# Revit family: 62172
name_source: partatom
category: Lighting Fixtures
revit_build: Autodesk Revit 2018 (Build: 20170223_1515(x64)
units: mm (PartAtom-declared; Revit-internal decimal feet)

## family parameters
Cut with Voids When Loaded = No
Host = Face
Light Source = Yes
OmniClass Number = 23.80.70.00
OmniClass Title = Lighting
Part Type = Normal
Room Calculation Point = No
Round Connector Dimension = Use Diameter
Shared = No

## types (1)
- 0062172 KUBIXX 4000K 47KLM AISLE  SSA N
    Apparent Load = 276 VA
    Assembly Code = D5020200
    AssetType = Fixed
    ClassificationName = Uniclass2015
    ClassificationValue = EF_70_80
    Color Filter = 16777215
    Cost = 0 $
    Default Elevation = 1219 mm
    Description = Logistics and Industry high bay luminaire with wide optics to provide homogenous light distribution for open space areas. 48300lumens, 276W, 175lm/W, 4000K, CRI80, wide beam optic, SylSmart SSA dimmable, 3 step MacAdam ellipse, grey finish (RAL7012), Class 1, 220-240V, IP65, IK06.
    Dimming Lamp Color Temperature Shift = <None>
    DocumentationLiterature = http://www.sylvania-lighting.com
    ElectricShockClassification = 175
    Emit Shape Visible in Rendering = No
    Emit from Circle Diameter = 610 mm
    IfcExportAs = Class I
    IfcExportType = IfcLightFixtureType
    ImpactProtectionIndex = IfcLightFixtureType
    IngressProtection = IfcLightFixtureType
    InputNominalFrequency = 4000
    InputVoltage = 0
    LampColourRenderingIndex = 16500
    LampColourTemperature = LED
    LampMacAdamStep = 80
    LampNominalLuminous = 4000 K
    LightOutputRatio = LED
    LuminaireType = 0
    ManufacturerName = 175 lm/W
    Material = Feilo Sylvania
    Material_1_SYL = <By Category>
    Material_2_SYL = <By Category>
    Material_3_SYL = <By Category>
    Material_4_SYL = <By Category>
    Model = KubiXx 4000K 47KLM AISLE  SSA N
    ModelNumber = 0062172
    ModelReference = KubiXx 4000K 47KLM AISLE  SSA N
    Name = KubiXx 4000K 47KLM AISLE  SSA N
    NominalDepth = 650 mm  [stored 2.13255 ft]
    NominalHeight = 94 mm  [stored 0.308399 ft]
    NominalLength = 460 mm  [stored 1.50919 ft]
    Photometric Web File = 0062172.IES
    PowerConsumption = Lighting
    PowerFactor = 0
    Suspension height = 3000 mm  [stored 9.84252 ft]
    Tilt Angle = -90.00°
    Total Length = 732 mm
    Total length = 760 mm
    Type Image = <None>
    TypeName = KubiXx 4000K 47KLM AISLE  SSA N
    URL = 0
    Voltage = 0 V
    WarrantyDescription = http://www.sylvania-lighting.com

note: [stored X ft] marks values corroborated as IEEE doubles in the binary element streams (Revit-internal decimal feet)

## geometry (parser evidence)
native form markers: Sweep x3
no freeform markers — native parametric forms only
